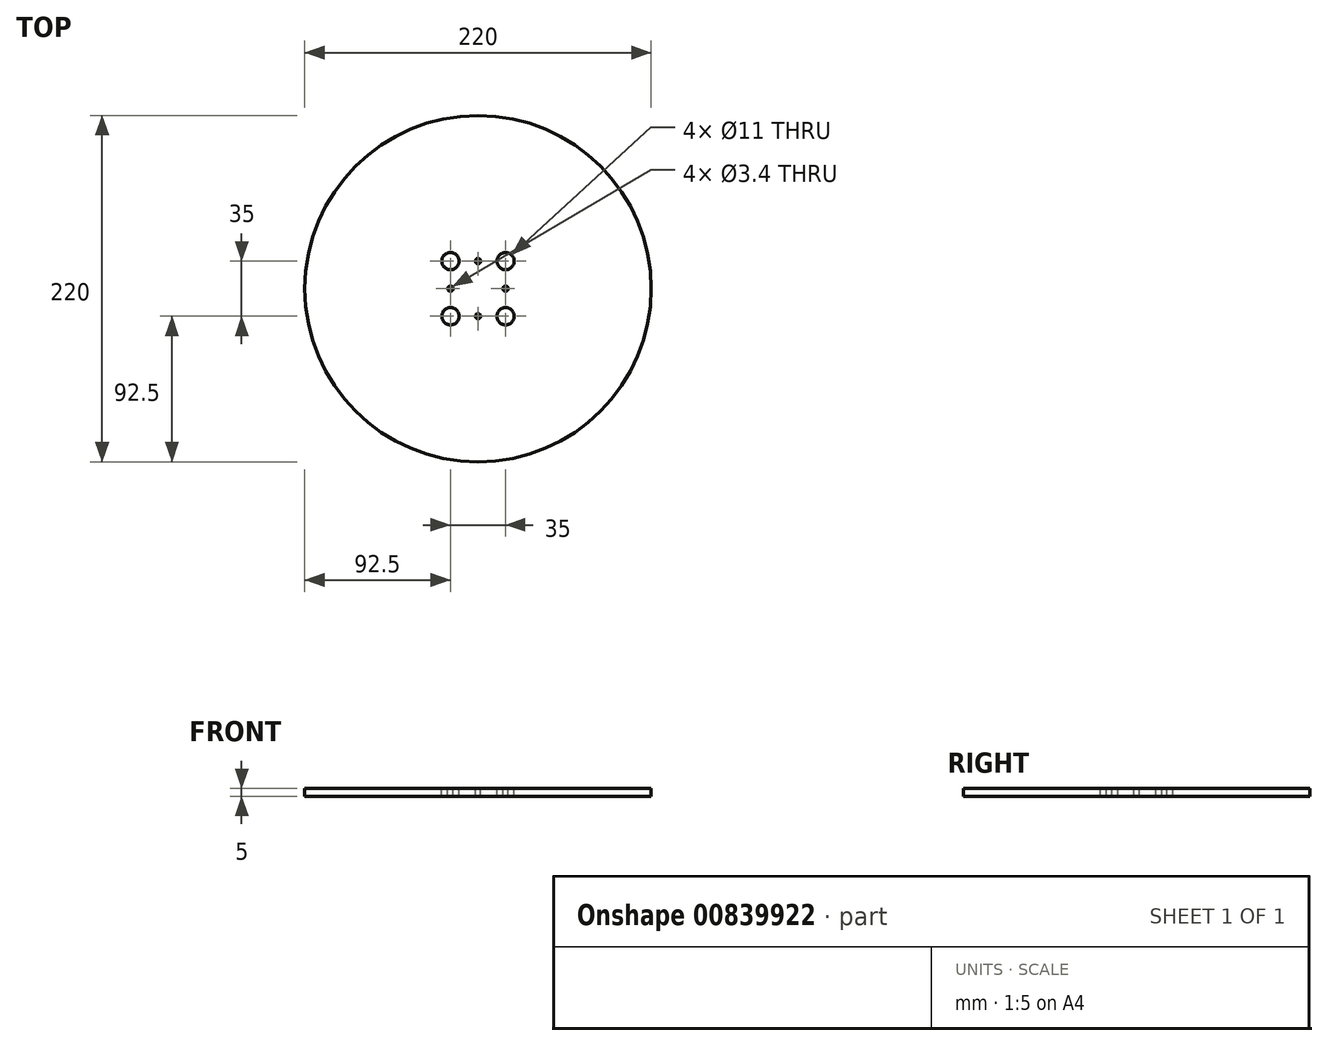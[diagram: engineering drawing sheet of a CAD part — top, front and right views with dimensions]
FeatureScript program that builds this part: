
annotation { "Feature Type Name" : "Feature", "Feature Type Description" : "" }
export const myFeature = defineFeature(function(context is Context, id is Id, definition is map)
    precondition{}
    {
        {
            var Q0;
            Q0=qCreatedBy(makeId("Top.planeOp"),FACE);
            var sketch = newSketch(context, id + "F0", { "sketchPlane" : qUnion([Q0])});
            skCircle(sketch, "E0", {"center": v(0, 0) * mm, "radius": 5 * mm});
            skSolve(sketch);
        }
        {
            var Q0;
            Q0=makeQuery(id+"F0.imprint","IMPRINT",FACE,{"disambiguationData":[TD([[makeQuery(id+"F0.imprint","IMPRINT",EDGE,{"derivedFrom":sQuery(id+"F0.wireOp",EDGE,"E0")}),1.0]])]});
            extrude(context, id + "F1", {"entities" : qUnion([Q0]), "depth" : 150 * mm, "offsetDistance" : 25 * mm});
        }
        {
            var Q0;
            Q0=makeQuery(id+"F1.opExtrude","CAP_FACE",FACE,{"disambiguationData":[OSD([sQuery(id+"F0.wireOp",EDGE,"E0")])],"isStart":false});
            var sketch = newSketch(context, id + "F2", { "sketchPlane" : qUnion([Q0])});
            skSolve(sketch);
        }
        {
            var Q0;
            Q0=makeQuery(id+"F2.imprint","IMPRINT",FACE,{"disambiguationData":[TD([[makeQuery(id+"F2.imprint","IMPRINT",EDGE,{"derivedFrom":makeQuery(id+"F1.opExtrude","CAP_EDGE",EDGE,{"disambiguationData":[OSD([sQuery(id+"F0.wireOp",EDGE,"E0")])],"isStart":false})}),1.0]])]});
            extrude(context, id + "F3", {"entities" : qUnion([Q0]), "operationType" : NewBodyOperationType.REMOVE, "oppositeDirection" : true, "depth" : 95 * mm, "offsetDistance" : 25 * mm});
        }
        {
            var Q0;
            Q0=makeQuery(id+"F3.boolean.opBoolean","COPY",FACE,{"derivedFrom":makeQuery(id+"F3.opExtrude","CAP_FACE",FACE,{"disambiguationData":[OSD([sQuery(id+"F0.wireOp",EDGE,"E0")])],"isStart":false})});
            var sketch = newSketch(context, id + "F4", { "sketchPlane" : qUnion([Q0])});
            skCircle(sketch, "E1", {"center": v(0, 0) * mm, "radius": 32.5 * mm});
            skSolve(sketch);
        }
        {
            var Q0;
            Q0=makeQuery(id+"F4.imprint","IMPRINT",FACE,{"disambiguationData":[TD([[makeQuery(id+"F4.imprint","IMPRINT",EDGE,{"derivedFrom":sQuery(id+"F4.wireOp",EDGE,"E1")}),1.0]])]});
            extrude(context, id + "F5", {"entities" : qUnion([Q0]), "operationType" : NewBodyOperationType.ADD, "oppositeDirection" : true, "depth" : 5 * mm, "offsetDistance" : 25 * mm});
        }
        {
            var Q0;
            {var subQ0=sQuery(id+"F0.wireOp",EDGE,"E0");Q0=makeQuery(id+"F5.boolean.opBoolean","MERGE",FACE,{"derivedFrom":[makeQuery(id+"F3.boolean.opBoolean","COPY",FACE,{"derivedFrom":makeQuery(id+"F3.opExtrude","CAP_FACE",FACE,{"disambiguationData":[OSD([subQ0])],"isStart":false})}),makeQuery(id+"F5.opExtrude","CAP_FACE",FACE,{"disambiguationData":[OSD([subQ0,sQuery(id+"F4.wireOp",EDGE,"E1")])],"isStart":true})]});}
            var sketch = newSketch(context, id + "F6", { "sketchPlane" : qUnion([Q0])});
            skLineSegment(sketch, "E2.bottom", {"start": v(17.5, 17.5) * mm, "end": v(-17.5, 17.5) * mm});
            skLineSegment(sketch, "E2.top", {"start": v(17.5, -17.5) * mm, "end": v(-17.5, -17.5) * mm});
            skLineSegment(sketch, "E2.left", {"start": v(17.5, 17.5) * mm, "end": v(17.5, -17.5) * mm});
            skLineSegment(sketch, "E2.right", {"start": v(-17.5, 17.5) * mm, "end": v(-17.5, -17.5) * mm});
            skPoint(sketch, "E2.middle", {"position": v(0, 0) * mm});
            skSolve(sketch);
        }
        {
            var Q0;
            Q0=sQuery(id+"F6.wireOp",VERTEX,"E2.top.start");
            var Q1;
            Q1=sQuery(id+"F6.wireOp",VERTEX,"E2.top.end");
            var Q2;
            Q2=sQuery(id+"F6.wireOp",VERTEX,"E2.bottom.end");
            var Q3;
            Q3=sQuery(id+"F6.wireOp",VERTEX,"E2.bottom.start");
            var Q4;
            Q4=makeQuery(id+"F1.opExtrude","SWEPT_BODY",BODY,{"disambiguationData":[OSD([sQuery(id+"F0.wireOp",EDGE,"E0")])]});
            hole(context, id + "F7", {"style" : HoleStyle.SIMPLE, "endStyle" : HoleEndStyle.THROUGH, "holeDiameter" : 11 * mm, "majorDiameter" : 5 * mm, "isTappedThrough" : true, "tappedDepth" : 12 * mm, "tapClearance" : 3, "locations" : qUnion([Q0, Q1, Q2, Q3]), "scope" : qUnion([Q4])});
        }
        {
            var Q0;
            Q0=makeQuery(id+"F1.opExtrude","CAP_FACE",FACE,{"disambiguationData":[OSD([sQuery(id+"F0.wireOp",EDGE,"E0")])],"isStart":true});
            var sketch = newSketch(context, id + "F8", { "sketchPlane" : qUnion([Q0])});
            skSolve(sketch);
        }
        {
            var Q0;
            Q0 = qSketchRegion(id + "F8", true);
            var Q1;
            Q1=makeQuery(id+"F8.imprint","IMPRINT",FACE,{"disambiguationData":[TD([[makeQuery(id+"F8.imprint","IMPRINT",EDGE,{"derivedFrom":makeQuery(id+"F1.opExtrude","CAP_EDGE",EDGE,{"disambiguationData":[OSD([sQuery(id+"F0.wireOp",EDGE,"E0")])],"isStart":true})}),-1.0]])]});
            extrude(context, id + "F9", {"entities" : qUnion([Q0, Q1]), "operationType" : NewBodyOperationType.REMOVE, "oppositeDirection" : true, "depth" : 50 * mm, "offsetDistance" : 25 * mm});
        }
        {
            var Q0;
            {var subQ0=sQuery(id+"F0.wireOp",EDGE,"E0");Q0=makeQuery(id+"F9.boolean.opBoolean","MERGE",FACE,{"derivedFrom":[makeQuery(id+"F5.opExtrude","CAP_FACE",FACE,{"disambiguationData":[OSD([subQ0,sQuery(id+"F4.wireOp",EDGE,"E1")])],"isStart":false}),makeQuery(id+"F9.opExtrude","CAP_FACE",FACE,{"disambiguationData":[OSD([subQ0])],"isStart":false})]});}
            var sketch = newSketch(context, id + "F10", { "sketchPlane" : qUnion([Q0])});
            skCircle(sketch, "E3", {"center": v(0, 0) * mm, "radius": 63.87 * mm});
            skCircle(sketch, "E4", {"center": v(0, 0) * mm, "radius": 125 * mm});
            skSolve(sketch);
        }
        {
            var Q0;
            Q0=makeQuery(id+"F10.imprint","IMPRINT",FACE,{"disambiguationData":[TD([[makeQuery(id+"F10.imprint","IMPRINT",EDGE,{"derivedFrom":sQuery(id+"F10.wireOp",EDGE,"E3")}),1.0]])]});
            var Q1;
            Q1=makeQuery(id+"F10.imprint","IMPRINT",FACE,{"disambiguationData":[TD([[makeQuery(id+"F10.imprint","IMPRINT",EDGE,{"derivedFrom":sQuery(id+"F10.wireOp",EDGE,"E3")}),-1.0]])]});
            extrude(context, id + "F11", {"entities" : qUnion([Q0, Q1]), "oppositeDirection" : true, "depth" : 5 * mm, "offsetDistance" : 25 * mm});
        }
        {
            var Q0;
            Q0=makeQuery(id+"F11.opExtrude","SWEPT_BODY",BODY,{"disambiguationData":[OSD([sQuery(id+"F4.wireOp",EDGE,"E1"),sQuery(id+"F10.wireOp",EDGE,"E4")])]});
            deleteBodies(context, id + "F12", {"entities" : qUnion([Q0])});
        }
        {
            var Q0;
            {var subQ0=sQuery(id+"F0.wireOp",EDGE,"E0");Q0=makeQuery(id+"F5.boolean.opBoolean","MERGE",FACE,{"derivedFrom":[makeQuery(id+"F3.boolean.opBoolean","COPY",FACE,{"derivedFrom":makeQuery(id+"F3.opExtrude","CAP_FACE",FACE,{"disambiguationData":[OSD([subQ0])],"isStart":false})}),makeQuery(id+"F5.opExtrude","CAP_FACE",FACE,{"disambiguationData":[OSD([subQ0,sQuery(id+"F4.wireOp",EDGE,"E1")])],"isStart":true})]});}
            var sketch = newSketch(context, id + "F13", { "sketchPlane" : qUnion([Q0])});
            skCircle(sketch, "E5", {"center": v(0, 0) * mm, "radius": 110 * mm});
            skCircle(sketch, "E6", {"center": v(-17.5, -17.5) * mm, "radius": 5.5 * mm});
            skCircle(sketch, "E7", {"center": v(-17.5, 17.5) * mm, "radius": 5.5 * mm});
            skCircle(sketch, "E8", {"center": v(17.5, 17.5) * mm, "radius": 5.5 * mm});
            skCircle(sketch, "E9", {"center": v(17.5, -17.5) * mm, "radius": 5.5 * mm});
            skSolve(sketch);
        }
        {
            var Q0;
            Q0=makeQuery(id+"F13.imprint","IMPRINT",FACE,{"disambiguationData":[TD([[makeQuery(id+"F13.imprint","IMPRINT",EDGE,{"derivedFrom":sQuery(id+"F13.wireOp",EDGE,"E5")}),1.0]])]});
            var Q1;
            Q1=makeQuery(id+"F13.imprint","IMPRINT",FACE,{"disambiguationData":[TD([[makeQuery(id+"F13.imprint","IMPRINT",EDGE,{"derivedFrom":sQuery(id+"F13.wireOp",EDGE,"E6")}),-1.0]])]});
            extrude(context, id + "F14", {"entities" : qUnion([Q0, Q1]), "operationType" : NewBodyOperationType.ADD, "depth" : 5 * mm, "offsetDistance" : 25 * mm});
        }
        {
            var Q0;
            {var subQ0=sQuery(id+"F0.wireOp",EDGE,"E0");Q0=makeQuery(id+"F9.boolean.opBoolean","MERGE",FACE,{"derivedFrom":[makeQuery(id+"F5.opExtrude","CAP_FACE",FACE,{"disambiguationData":[OSD([subQ0,sQuery(id+"F4.wireOp",EDGE,"E1")])],"isStart":false}),makeQuery(id+"F9.opExtrude","CAP_FACE",FACE,{"disambiguationData":[OSD([subQ0])],"isStart":false})]});}
            extrude(context, id + "F15", {"entities" : qUnion([Q0]), "operationType" : NewBodyOperationType.REMOVE, "oppositeDirection" : true, "depth" : 5 * mm, "offsetDistance" : 25 * mm});
        }
        {
            var Q0;
            Q0=makeQuery(id+"F14.opExtrude","CAP_FACE",FACE,{"disambiguationData":[OSD([sQuery(id+"F13.wireOp",EDGE,"E5"),sQuery(id+"F13.wireOp",EDGE,"E6"),sQuery(id+"F13.wireOp",EDGE,"E7"),sQuery(id+"F13.wireOp",EDGE,"E8"),sQuery(id+"F13.wireOp",EDGE,"E9")])],"isStart":false});
            var sketch = newSketch(context, id + "F16", { "sketchPlane" : qUnion([Q0])});
            skLineSegment(sketch, "E10.bottom", {"start": v(17.5, 17.5) * mm, "end": v(-17.5, 17.5) * mm});
            skLineSegment(sketch, "E10.top", {"start": v(17.5, -17.5) * mm, "end": v(-17.5, -17.5) * mm});
            skLineSegment(sketch, "E10.left", {"start": v(17.5, 17.5) * mm, "end": v(17.5, -17.5) * mm});
            skLineSegment(sketch, "E10.right", {"start": v(-17.5, 17.5) * mm, "end": v(-17.5, -17.5) * mm});
            skPoint(sketch, "E10.middle", {"position": v(0, 0) * mm});
            skPoint(sketch, "E11", {"position": v(0, 17.5) * mm});
            skPoint(sketch, "E12", {"position": v(-17.5, 0) * mm});
            skPoint(sketch, "E13", {"position": v(0, -17.5) * mm});
            skPoint(sketch, "E14", {"position": v(17.5, 0) * mm});
            skSolve(sketch);
        }
        {
            var Q0;
            Q0=sQuery(id+"F16.wireOp",VERTEX,"E11");
            var Q1;
            Q1=sQuery(id+"F16.wireOp",VERTEX,"E12");
            var Q2;
            Q2=sQuery(id+"F16.wireOp",VERTEX,"E13");
            var Q3;
            Q3=sQuery(id+"F16.wireOp",VERTEX,"E14");
            var Q4;
            Q4=makeQuery(id+"F1.opExtrude","SWEPT_BODY",BODY,{"disambiguationData":[OSD([sQuery(id+"F0.wireOp",EDGE,"E0")])]});
            hole(context, id + "F17", {"style" : HoleStyle.SIMPLE, "endStyle" : HoleEndStyle.THROUGH, "standardTappedOrClearance" : lookupTablePath({ "fit" : "Normal", "standard" : "ISO", "size" : "M3", "type" : "Clearance" }), "standardBlindInLast" : lookupTablePath({ "fit" : "Normal", "standard" : "ISO", "size" : "M3", "type" : "Clearance" }), "holeDiameter" : 3.4 * mm, "majorDiameter" : 5 * mm, "isTappedThrough" : true, "tappedDepth" : 12 * mm, "tapClearance" : 3, "locations" : qUnion([Q0, Q1, Q2, Q3]), "scope" : qUnion([Q4])});
        }
    });
